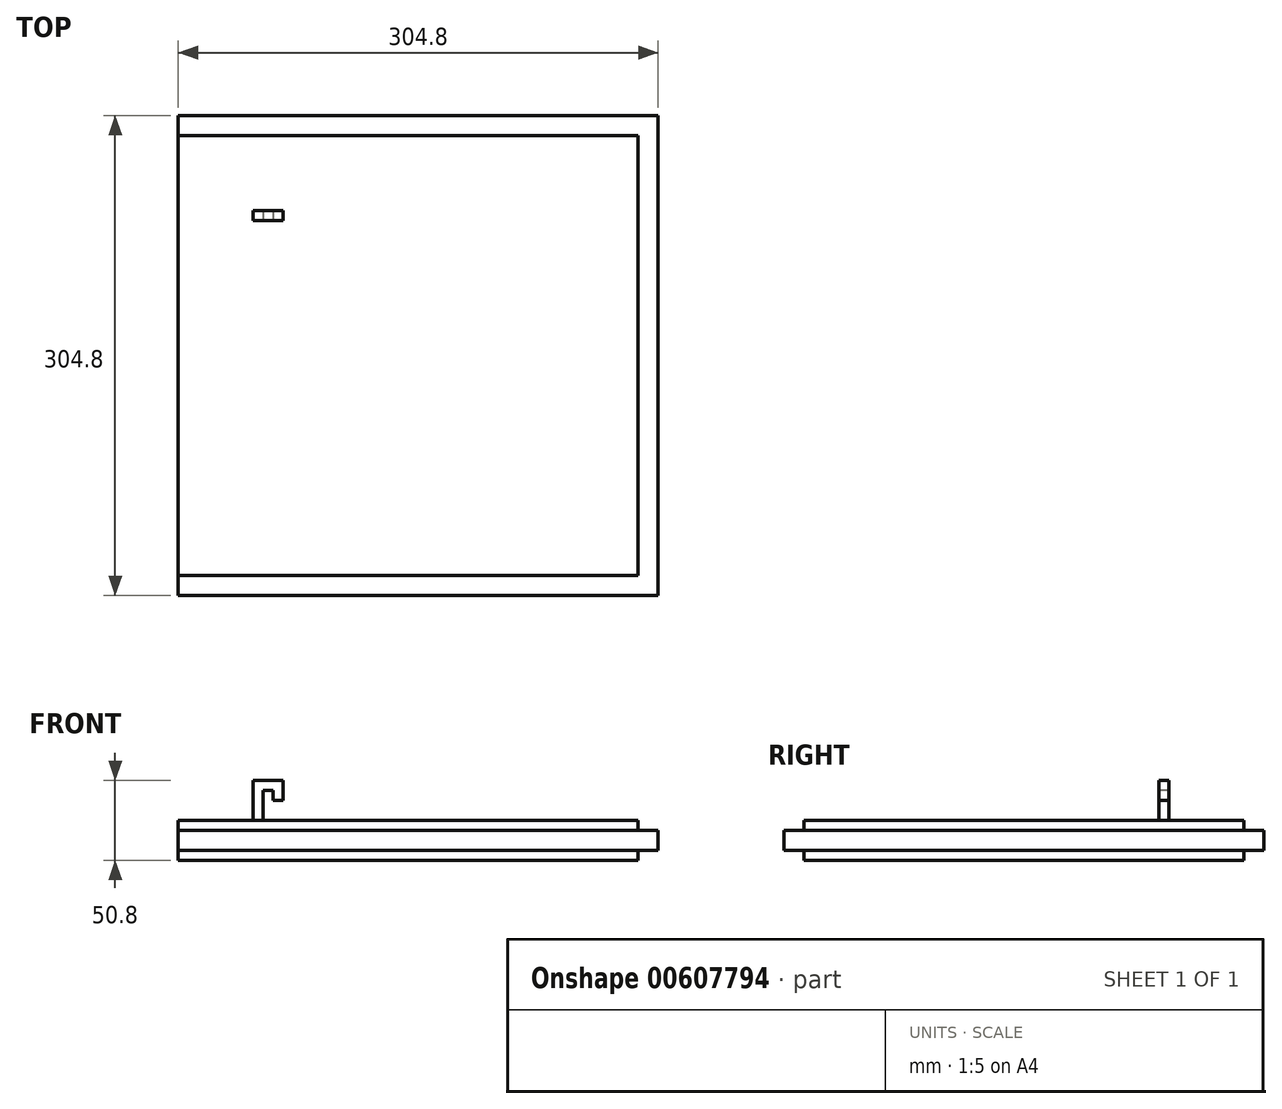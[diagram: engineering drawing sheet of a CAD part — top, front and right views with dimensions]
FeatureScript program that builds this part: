
annotation { "Feature Type Name" : "Feature", "Feature Type Description" : "" }
export const myFeature = defineFeature(function(context is Context, id is Id, definition is map)
    precondition{}
    {
        {
            var Q0;
            Q0=qCreatedBy(makeId("Top.planeOp"),FACE);
            var sketch = newSketch(context, id + "F0", { "sketchPlane" : qUnion([Q0])});
            skLineSegment(sketch, "E0.bottom", {"start": v(146.05, -139.7) * mm, "end": v(-146.05, -139.7) * mm});
            skLineSegment(sketch, "E0.top", {"start": v(146.05, 139.7) * mm, "end": v(-146.05, 139.7) * mm});
            skLineSegment(sketch, "E0.left", {"start": v(146.05, -139.7) * mm, "end": v(146.05, 139.7) * mm});
            skLineSegment(sketch, "E0.right", {"start": v(-146.05, -139.7) * mm, "end": v(-146.05, 139.7) * mm});
            skPoint(sketch, "E0.middle", {"position": v(0, 0) * mm});
            skSolve(sketch);
        }
        {
            var Q0;
            Q0=makeQuery(id+"F0.imprint","IMPRINT",FACE,{"disambiguationData":[TD([[makeQuery(id+"F0.imprint","IMPRINT",EDGE,{"derivedFrom":sQuery(id+"F0.wireOp",EDGE,"E0.bottom")}),-1.0]])]});
            extrude(context, id + "F1", {"entities" : qUnion([Q0]), "depth" : 25.4 * mm, "offsetDistance" : 25.4 * mm});
        }
        {
            var Q0;
            Q0=makeQuery(id+"F1.opExtrude","SWEPT_FACE",FACE,{"disambiguationData":[OSD([sQuery(id+"F0.wireOp",EDGE,"E0.left")])]});
            var sketch = newSketch(context, id + "F2", { "sketchPlane" : qUnion([Q0])});
            skLineSegment(sketch, "E1", {"start": v(139.7, 25.4) * mm, "end": v(139.7, 19.05) * mm});
            skLineSegment(sketch, "E2", {"start": v(139.7, 19.05) * mm, "end": v(139.7, 6.35) * mm});
            skLineSegment(sketch, "E3", {"start": v(139.7, 6.35) * mm, "end": v(-139.7, 6.35) * mm});
            skLineSegment(sketch, "E4", {"start": v(-139.7, 6.35) * mm, "end": v(-139.7, 19.05) * mm});
            skLineSegment(sketch, "E5", {"start": v(-139.7, 19.05) * mm, "end": v(139.7, 19.05) * mm});
            skSolve(sketch);
        }
        {
            var Q0;
            Q0=makeQuery(id+"F2.imprint","IMPRINT",FACE,{"disambiguationData":[TD([[makeQuery(id+"F2.imprint","IMPRINT",EDGE,{"derivedFrom":sQuery(id+"F2.wireOp",EDGE,"E2")}),-1.0]])]});
            extrude(context, id + "F3", {"entities" : qUnion([Q0]), "operationType" : NewBodyOperationType.ADD, "depth" : 12.7 * mm, "offsetDistance" : 25.4 * mm});
        }
        {
            var Q0;
            Q0=makeQuery(id+"F1.opExtrude","SWEPT_FACE",FACE,{"disambiguationData":[OSD([sQuery(id+"F0.wireOp",EDGE,"E0.right")])]});
            var sketch = newSketch(context, id + "F4", { "sketchPlane" : qUnion([Q0])});
            skLineSegment(sketch, "E6", {"start": v(139.7, 25.4) * mm, "end": v(139.7, 19.05) * mm});
            skLineSegment(sketch, "E7", {"start": v(139.7, 19.05) * mm, "end": v(139.7, 6.35) * mm});
            skLineSegment(sketch, "E8", {"start": v(139.7, 6.35) * mm, "end": v(-139.7, 6.35) * mm});
            skLineSegment(sketch, "E9", {"start": v(-139.7, 6.35) * mm, "end": v(-139.7, 19.05) * mm});
            skLineSegment(sketch, "E10", {"start": v(-139.7, 19.05) * mm, "end": v(139.7, 19.05) * mm});
            skSolve(sketch);
        }
        {
            var Q0;
            Q0=makeQuery(id+"FlfyzCArbw85mND_1.boolean.opBoolean","MERGE",FACE,{"derivedFrom":[makeQuery(id+"F3.boolean.opBoolean","MERGE",FACE,{"derivedFrom":[makeQuery(id+"F1.opExtrude","SWEPT_FACE",FACE,{"disambiguationData":[OSD([sQuery(id+"F0.wireOp",EDGE,"E0.bottom")])]}),makeQuery(id+"F3.opExtrude","SWEPT_FACE",FACE,{"disambiguationData":[OSD([sQuery(id+"F2.wireOp",EDGE,"E4")])]})]}),makeQuery(id+"FlfyzCArbw85mND_1.opExtrude","SWEPT_FACE",FACE,{"disambiguationData":[OSD([sQuery(id+"F4.wireOp",EDGE,"E7")])]})]});
            var sketch = newSketch(context, id + "F5", { "sketchPlane" : qUnion([Q0])});
            skLineSegment(sketch, "E11.bottom", {"start": v(-158.75, 19.05) * mm, "end": v(158.75, 19.05) * mm});
            skLineSegment(sketch, "E11.top", {"start": v(-158.75, 6.35) * mm, "end": v(158.75, 6.35) * mm});
            skLineSegment(sketch, "E11.left", {"start": v(-158.75, 19.05) * mm, "end": v(-158.75, 6.35) * mm});
            skLineSegment(sketch, "E11.right", {"start": v(158.75, 19.05) * mm, "end": v(158.75, 6.35) * mm});
            skSolve(sketch);
        }
        {
            var Q0;
            Q0=makeQuery(id+"F1.opExtrude","CAP_FACE",FACE,{"disambiguationData":[OSD([sQuery(id+"F0.wireOp",EDGE,"E0.bottom"),sQuery(id+"F0.wireOp",EDGE,"E0.top"),sQuery(id+"F0.wireOp",EDGE,"E0.left"),sQuery(id+"F0.wireOp",EDGE,"E0.right")])],"isStart":false});
            var sketch = newSketch(context, id + "F6", { "sketchPlane" : qUnion([Q0])});
            skLineSegment(sketch, "E12", {"start": v(-146.05, 139.7) * mm, "end": v(-146.05, 88.9) * mm});
            skLineSegment(sketch, "E13", {"start": v(-146.05, 88.9) * mm, "end": v(-95.25, 88.9) * mm});
            skLineSegment(sketch, "E14.bottom", {"start": v(-92.07, 85.72) * mm, "end": v(-98.42, 85.72) * mm});
            skLineSegment(sketch, "E14.top", {"start": v(-92.07, 92.07) * mm, "end": v(-98.42, 92.07) * mm});
            skLineSegment(sketch, "E14.left", {"start": v(-92.07, 85.72) * mm, "end": v(-92.07, 92.07) * mm});
            skLineSegment(sketch, "E14.right", {"start": v(-98.42, 85.72) * mm, "end": v(-98.42, 92.07) * mm});
            skPoint(sketch, "E14.middle", {"position": v(-95.25, 88.9) * mm});
            skSolve(sketch);
        }
        {
            var Q0;
            {var subQ1=sQuery(id+"F6.wireOp",EDGE,"E14.bottom");Q0=makeQuery(id+"F6.imprint","IMPRINT",FACE,{"disambiguationData":[TD([[makeQuery(id+"F6.imprint","IMPRINT",EDGE,{"derivedFrom":subQ1}),-1.0]])]});}
            extrude(context, id + "F7", {"entities" : qUnion([Q0]), "operationType" : NewBodyOperationType.ADD, "depth" : 25.4 * mm, "offsetDistance" : 25.4 * mm});
        }
        {
            var Q0;
            Q0=makeQuery(id+"F7.opExtrude","SWEPT_FACE",FACE,{"disambiguationData":[OSD([sQuery(id+"F6.wireOp",EDGE,"E14.left")])]});
            var sketch = newSketch(context, id + "F8", { "sketchPlane" : qUnion([Q0])});
            skLineSegment(sketch, "E15.bottom", {"start": v(92.07, 50.8) * mm, "end": v(85.72, 50.8) * mm});
            skLineSegment(sketch, "E15.top", {"start": v(92.07, 44.45) * mm, "end": v(85.72, 44.45) * mm});
            skLineSegment(sketch, "E15.left", {"start": v(92.07, 50.8) * mm, "end": v(92.07, 44.45) * mm});
            skLineSegment(sketch, "E15.right", {"start": v(85.72, 50.8) * mm, "end": v(85.72, 44.45) * mm});
            skSolve(sketch);
        }
        {
            var Q0;
            Q0=makeQuery(id+"F8.imprint","IMPRINT",FACE,{"disambiguationData":[TD([[makeQuery(id+"F8.imprint","IMPRINT",EDGE,{"derivedFrom":sQuery(id+"F8.wireOp",EDGE,"E15.bottom")}),-1.0]])]});
            extrude(context, id + "F9", {"entities" : qUnion([Q0]), "operationType" : NewBodyOperationType.ADD, "depth" : 12.7 * mm, "offsetDistance" : 25.4 * mm});
        }
        {
            var Q0;
            Q0=makeQuery(id+"F9.opExtrude","SWEPT_FACE",FACE,{"disambiguationData":[OSD([sQuery(id+"F8.wireOp",EDGE,"E15.top")])]});
            var sketch = newSketch(context, id + "F10", { "sketchPlane" : qUnion([Q0])});
            skLineSegment(sketch, "E16.bottom", {"start": v(-79.37, -92.07) * mm, "end": v(-85.72, -92.07) * mm});
            skLineSegment(sketch, "E16.top", {"start": v(-79.37, -85.72) * mm, "end": v(-85.72, -85.72) * mm});
            skLineSegment(sketch, "E16.left", {"start": v(-79.37, -92.07) * mm, "end": v(-79.37, -85.72) * mm});
            skLineSegment(sketch, "E16.right", {"start": v(-85.72, -92.07) * mm, "end": v(-85.72, -85.72) * mm});
            skSolve(sketch);
        }
        {
            var Q0;
            Q0=makeQuery(id+"F10.imprint","IMPRINT",FACE,{"disambiguationData":[TD([[makeQuery(id+"F10.imprint","IMPRINT",EDGE,{"derivedFrom":sQuery(id+"F10.wireOp",EDGE,"E16.bottom")}),-1.0]])]});
            extrude(context, id + "F11", {"entities" : qUnion([Q0]), "operationType" : NewBodyOperationType.ADD, "depth" : 6.35 * mm, "offsetDistance" : 25.4 * mm});
        }
        {
            var Q0;
            Q0=makeQuery(id+"FlfyzCArbw85mND_1.boolean.opBoolean","MERGE",FACE,{"derivedFrom":[makeQuery(id+"F3.boolean.opBoolean","MERGE",FACE,{"derivedFrom":[makeQuery(id+"F1.opExtrude","SWEPT_FACE",FACE,{"disambiguationData":[OSD([sQuery(id+"F0.wireOp",EDGE,"E0.top")])]}),makeQuery(id+"F3.opExtrude","SWEPT_FACE",FACE,{"disambiguationData":[OSD([sQuery(id+"F2.wireOp",EDGE,"E2")])]})]}),makeQuery(id+"FlfyzCArbw85mND_1.opExtrude","SWEPT_FACE",FACE,{"disambiguationData":[OSD([sQuery(id+"F4.wireOp",EDGE,"E9")])]})]});
            var sketch = newSketch(context, id + "F12", { "sketchPlane" : qUnion([Q0])});
            skLineSegment(sketch, "E17.bottom", {"start": v(-158.75, 6.35) * mm, "end": v(146.05, 6.35) * mm});
            skLineSegment(sketch, "E17.top", {"start": v(-158.75, 19.05) * mm, "end": v(146.05, 19.05) * mm});
            skLineSegment(sketch, "E17.left", {"start": v(-158.75, 6.35) * mm, "end": v(-158.75, 19.05) * mm});
            skLineSegment(sketch, "E17.right", {"start": v(146.05, 6.35) * mm, "end": v(146.05, 19.05) * mm});
            skSolve(sketch);
        }
        {
            var Q0;
            {var subQ0=sQuery(id+"F12.wireOp",EDGE,"E17.left");Q0=makeQuery(id+"F12.imprint","IMPRINT",FACE,{"disambiguationData":[TD([[makeQuery(id+"F12.imprint","IMPRINT",EDGE,{"derivedFrom":subQ0}),1.0]])]});}
            extrude(context, id + "F13", {"entities" : qUnion([Q0]), "operationType" : NewBodyOperationType.ADD, "depth" : 12.7 * mm, "offsetDistance" : 25.4 * mm});
        }
        {
            var Q0;
            {var subQ0=sQuery(id+"F5.wireOp",EDGE,"E11.right");Q0=makeQuery(id+"F5.imprint","IMPRINT",FACE,{"disambiguationData":[TD([[makeQuery(id+"F5.imprint","IMPRINT",EDGE,{"derivedFrom":subQ0}),-1.0]])]});}
            extrude(context, id + "F14", {"entities" : qUnion([Q0]), "operationType" : NewBodyOperationType.ADD, "depth" : 12.7 * mm, "offsetDistance" : 25.4 * mm});
        }
    });
